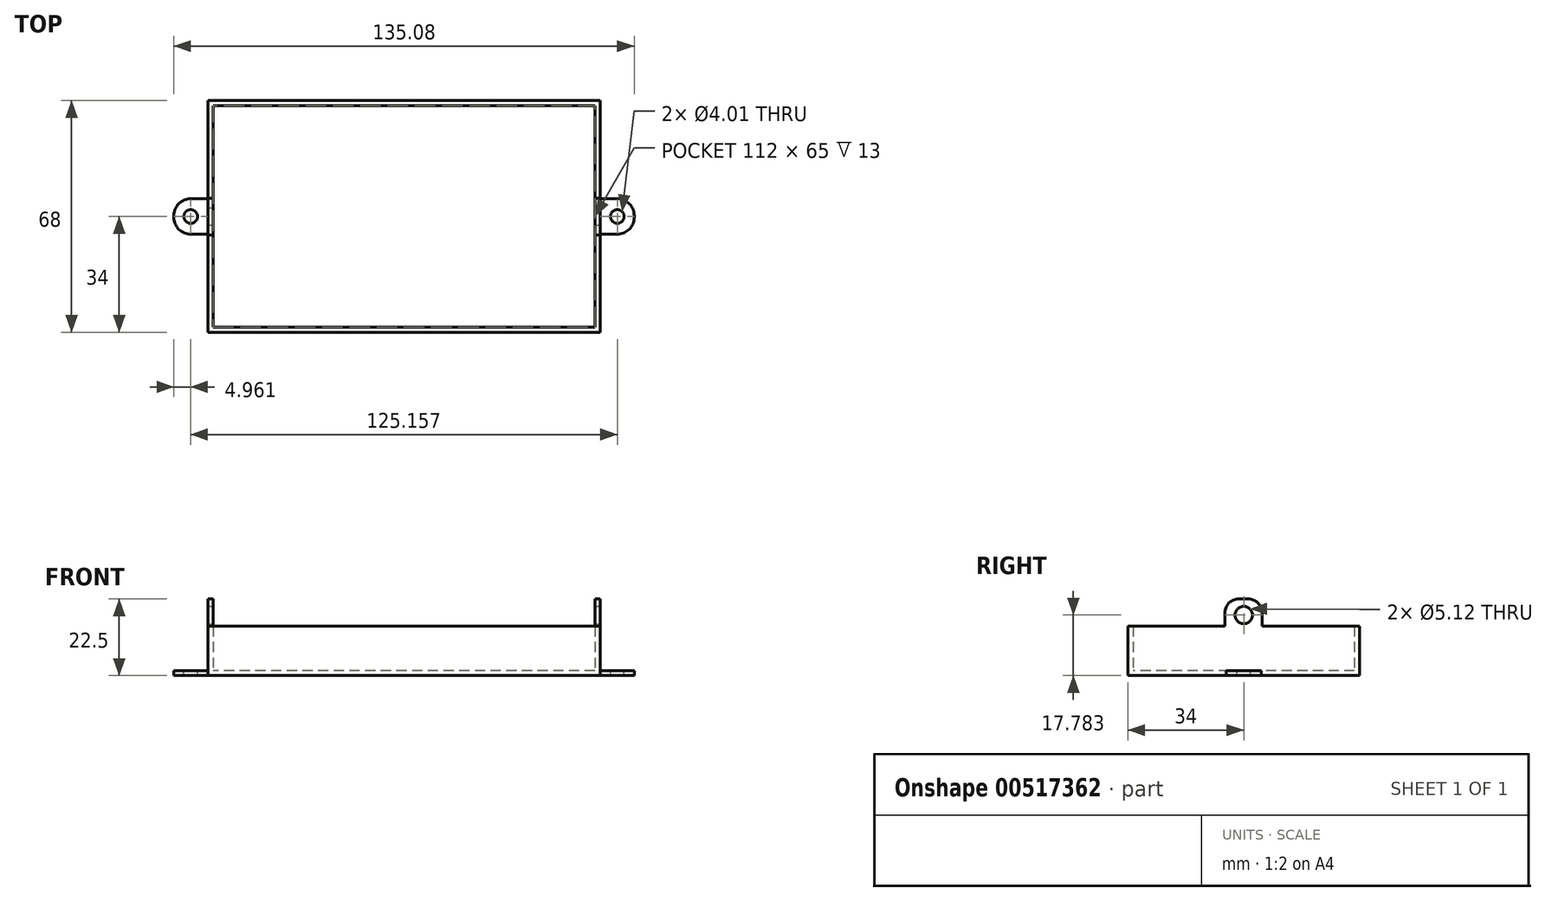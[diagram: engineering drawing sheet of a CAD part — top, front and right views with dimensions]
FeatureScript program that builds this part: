
annotation { "Feature Type Name" : "Feature", "Feature Type Description" : "" }
export const myFeature = defineFeature(function(context is Context, id is Id, definition is map)
    precondition{}
    {
        {
            var Q0;
            Q0=qCreatedBy(makeId("Top.planeOp"),FACE);
            var sketch = newSketch(context, id + "F0", { "sketchPlane" : qUnion([Q0])});
            skLineSegment(sketch, "E0.bottom", {"start": v(57.5, 34) * mm, "end": v(-57.5, 34) * mm});
            skLineSegment(sketch, "E0.top", {"start": v(57.5, -34) * mm, "end": v(-57.5, -34) * mm});
            skLineSegment(sketch, "E0.left", {"start": v(57.5, 34) * mm, "end": v(57.5, -34) * mm});
            skLineSegment(sketch, "E0.right", {"start": v(-57.5, 34) * mm, "end": v(-57.5, -34) * mm});
            skPoint(sketch, "E0.middle", {"position": v(0, 0) * mm});
            skLineSegment(sketch, "E1.top", {"start": v(57.5, 5.2) * mm, "end": v(67.54, 5.2) * mm});
            skLineSegment(sketch, "E1.left", {"start": v(57.5, 0) * mm, "end": v(57.5, 5.2) * mm});
            skLineSegment(sketch, "E1.right", {"start": v(67.54, 0) * mm, "end": v(67.54, 5.2) * mm});
            skLineSegment(sketch, "E2.MirrorCS", {"start": v(57.5, -5.2) * mm, "end": v(67.54, -5.2) * mm});
            skLineSegment(sketch, "E3.MirrorCS", {"start": v(67.54, 0) * mm, "end": v(67.54, -5.2) * mm});
            skLineSegment(sketch, "E4.MirrorCS", {"start": v(-57.5, 5.2) * mm, "end": v(-67.54, 5.2) * mm});
            skLineSegment(sketch, "E5.MirrorCS", {"start": v(-67.54, 0) * mm, "end": v(-67.54, 5.2) * mm});
            skLineSegment(sketch, "E6.MirrorCS", {"start": v(-67.54, 0) * mm, "end": v(-67.54, -5.2) * mm});
            skLineSegment(sketch, "E7.MirrorCS", {"start": v(-57.5, -5.2) * mm, "end": v(-67.54, -5.2) * mm});
            skSolve(sketch);
        }
        {
            var Q0;
            {var subQ3=sQuery(id+"F0.wireOp",EDGE,"E0.bottom");Q0=makeQuery(id+"F0.imprint","IMPRINT",FACE,{"disambiguationData":[TD([[makeQuery(id+"F0.imprint","IMPRINT",EDGE,{"derivedFrom":subQ3}),1.0]])]});}
            var Q1;
            {var subQ0=sQuery(id+"F0.wireOp",EDGE,"E4.MirrorCS");Q1=makeQuery(id+"F0.imprint","IMPRINT",FACE,{"disambiguationData":[TD([[makeQuery(id+"F0.imprint","IMPRINT",EDGE,{"derivedFrom":subQ0}),1.0]])]});}
            var Q2;
            Q2=makeQuery(id+"F0.imprint","IMPRINT",FACE,{"disambiguationData":[TD([[makeQuery(id+"F0.imprint","IMPRINT",EDGE,{"derivedFrom":sQuery(id+"F0.wireOp",EDGE,"E1.top")}),-1.0]])]});
            extrude(context, id + "F1", {"entities" : qUnion([Q0, Q1, Q2]), "depth" : 1.5 * mm, "offsetDistance" : 25 * mm});
        }
        {
            var Q0;
            Q0=makeQuery(id+"F1.opExtrude","CAP_FACE",FACE,{"disambiguationData":[OSD([sQuery(id+"F0.wireOp",EDGE,"E0.bottom"),sQuery(id+"F0.wireOp",EDGE,"E0.top"),sQuery(id+"F0.wireOp",EDGE,"E0.left"),sQuery(id+"F0.wireOp",EDGE,"E0.right"),sQuery(id+"F0.wireOp",EDGE,"E1.top"),sQuery(id+"F0.wireOp",EDGE,"E1.right"),sQuery(id+"F0.wireOp",EDGE,"E2.MirrorCS"),sQuery(id+"F0.wireOp",EDGE,"E3.MirrorCS"),sQuery(id+"F0.wireOp",EDGE,"E4.MirrorCS"),sQuery(id+"F0.wireOp",EDGE,"E5.MirrorCS"),sQuery(id+"F0.wireOp",EDGE,"E6.MirrorCS"),sQuery(id+"F0.wireOp",EDGE,"E7.MirrorCS")])],"isStart":false});
            var sketch = newSketch(context, id + "F2", { "sketchPlane" : qUnion([Q0])});
            skLineSegment(sketch, "E8", {"start": v(-57.5, 5.2) * mm, "end": v(-57.5, -5.2) * mm});
            skLineSegment(sketch, "E9", {"start": v(57.5, -5.2) * mm, "end": v(57.5, 5.2) * mm});
            skLineSegment(sketch, "E10.0", {"start": v(56, 32.5) * mm, "end": v(56, 5.2) * mm});
            skLineSegment(sketch, "E10.1", {"start": v(56, -5.2) * mm, "end": v(56, 5.2) * mm});
            skLineSegment(sketch, "E10.2", {"start": v(56, 32.5) * mm, "end": v(-56, 32.5) * mm});
            skLineSegment(sketch, "E10.3", {"start": v(56, -5.2) * mm, "end": v(56, -32.5) * mm});
            skLineSegment(sketch, "E10.4", {"start": v(-56, 32.5) * mm, "end": v(-56, 5.2) * mm});
            skLineSegment(sketch, "E10.5", {"start": v(-56, 5.2) * mm, "end": v(-56, -5.2) * mm});
            skLineSegment(sketch, "E10.6", {"start": v(-56, -5.2) * mm, "end": v(-56, -32.5) * mm});
            skLineSegment(sketch, "E10.7", {"start": v(56, -32.5) * mm, "end": v(-56, -32.5) * mm});
            skSolve(sketch);
        }
        {
            var Q0;
            Q0=makeQuery(id+"F2.imprint","IMPRINT",FACE,{"disambiguationData":[TD([[makeQuery(id+"F2.imprint","IMPRINT",EDGE,{"derivedFrom":sQuery(id+"F2.wireOp",EDGE,"E8")}),1.0]])]});
            extrude(context, id + "F3", {"entities" : qUnion([Q0]), "operationType" : NewBodyOperationType.ADD, "depth" : 13 * mm, "offsetDistance" : 25 * mm});
        }
        {
            var Q0;
            {var subQ0=sQuery(id+"F0.wireOp",EDGE,"E6.MirrorCS");var subQ1=sQuery(id+"F0.wireOp",EDGE,"E5.MirrorCS");var subQ2=sQuery(id+"F0.wireOp",EDGE,"E0.right");var subQ3=sQuery(id+"F0.wireOp",EDGE,"E0.top");var subQ4=sQuery(id+"F0.wireOp",EDGE,"E7.MirrorCS");var subQ5=sQuery(id+"F0.wireOp",EDGE,"E4.MirrorCS");var subQ6=sQuery(id+"F0.wireOp",EDGE,"E0.bottom");Q0=makeQuery(id+"F3.boolean.opBoolean","SPLIT",FACE,{"disambiguationData":[TD([makeQuery(id+"F1.opExtrude","SWEPT_FACE",FACE,{"disambiguationData":[OSD([subQ5])]})])],"derivedFrom":makeQuery(id+"F1.opExtrude","CAP_FACE",FACE,{"disambiguationData":[OSD([subQ6,subQ3,sQuery(id+"F0.wireOp",EDGE,"E0.left"),subQ2,sQuery(id+"F0.wireOp",EDGE,"E1.top"),sQuery(id+"F0.wireOp",EDGE,"E1.right"),sQuery(id+"F0.wireOp",EDGE,"E2.MirrorCS"),sQuery(id+"F0.wireOp",EDGE,"E3.MirrorCS"),subQ5,subQ1,subQ0,subQ4])],"isStart":false})});}
            var sketch = newSketch(context, id + "F4", { "sketchPlane" : qUnion([Q0])});
            skCircle(sketch, "E11", {"center": v(-62.58, 0) * mm, "radius": 2 * mm});
            skPoint(sketch, "E11.centerSnap0", {"position": v(-67.54, 0) * mm});
            skCircle(sketch, "E12.MirrorC", {"center": v(62.58, 0) * mm, "radius": 2 * mm});
            skSolve(sketch);
        }
        {
            var Q0;
            Q0 = qSketchRegion(id + "F4", true);
            extrude(context, id + "F5", {"entities" : qUnion([Q0]), "operationType" : NewBodyOperationType.REMOVE, "oppositeDirection" : true, "depth" : 2 * mm, "offsetDistance" : 25 * mm});
        }
        {
            var Q0;
            Q0=makeQuery(id+"F1.opExtrude","SWEPT_EDGE",EDGE,{"disambiguationData":[OSD([sQuery(id+"F0.wireOp",EDGE,"E4.MirrorCS"),sQuery(id+"F0.wireOp",EDGE,"E5.MirrorCS")])]});
            var Q1;
            Q1=makeQuery(id+"F1.opExtrude","SWEPT_EDGE",EDGE,{"disambiguationData":[OSD([sQuery(id+"F0.wireOp",EDGE,"E6.MirrorCS"),sQuery(id+"F0.wireOp",EDGE,"E7.MirrorCS")])]});
            var Q2;
            Q2=makeQuery(id+"F1.opExtrude","SWEPT_EDGE",EDGE,{"disambiguationData":[OSD([sQuery(id+"F0.wireOp",EDGE,"E1.top"),sQuery(id+"F0.wireOp",EDGE,"E1.right")])]});
            var Q3;
            Q3=makeQuery(id+"F1.opExtrude","SWEPT_EDGE",EDGE,{"disambiguationData":[OSD([sQuery(id+"F0.wireOp",EDGE,"E2.MirrorCS"),sQuery(id+"F0.wireOp",EDGE,"E3.MirrorCS")])]});
            fillet(context, id + "F6", {"entities" : qUnion([Q0, Q1, Q2, Q3]), "radius" : 5 * mm, "tangentPropagation" : true, "allowEdgeOverflow" : false});
        }
        {
            var Q0;
            Q0=makeQuery(id+"F3.opExtrude","CAP_FACE",FACE,{"disambiguationData":[OSD([sQuery(id+"F0.wireOp",EDGE,"E0.bottom"),sQuery(id+"F0.wireOp",EDGE,"E0.top"),sQuery(id+"F0.wireOp",EDGE,"E0.left"),sQuery(id+"F0.wireOp",EDGE,"E0.right"),sQuery(id+"F2.wireOp",EDGE,"E8"),sQuery(id+"F2.wireOp",EDGE,"E9"),sQuery(id+"F2.wireOp",EDGE,"E10.0"),sQuery(id+"F2.wireOp",EDGE,"E10.1"),sQuery(id+"F2.wireOp",EDGE,"E10.2"),sQuery(id+"F2.wireOp",EDGE,"E10.3"),sQuery(id+"F2.wireOp",EDGE,"E10.4"),sQuery(id+"F2.wireOp",EDGE,"E10.5"),sQuery(id+"F2.wireOp",EDGE,"E10.6"),sQuery(id+"F2.wireOp",EDGE,"E10.7")])],"isStart":false});
            var sketch = newSketch(context, id + "F7", { "sketchPlane" : qUnion([Q0])});
            skLineSegment(sketch, "E13", {"start": v(-57.5, 5.36) * mm, "end": v(-56, 5.36) * mm});
            skLineSegment(sketch, "E14", {"start": v(-57.5, -5.5) * mm, "end": v(-56, -5.5) * mm});
            skLineSegment(sketch, "E15", {"start": v(-56, 5.36) * mm, "end": v(-56, -5.5) * mm});
            skLineSegment(sketch, "E16", {"start": v(-57.5, -5.5) * mm, "end": v(-57.5, 5.36) * mm});
            skLineSegment(sketch, "E17.MirrorCS", {"start": v(56, 5.36) * mm, "end": v(56, -5.5) * mm});
            skLineSegment(sketch, "E18.MirrorCS", {"start": v(57.5, -5.5) * mm, "end": v(57.5, 5.36) * mm});
            skLineSegment(sketch, "E19.MirrorCS", {"start": v(57.5, 5.36) * mm, "end": v(56, 5.36) * mm});
            skLineSegment(sketch, "E20.MirrorCS", {"start": v(57.5, -5.5) * mm, "end": v(56, -5.5) * mm});
            skSolve(sketch);
        }
        {
            var Q0;
            Q0 = qSketchRegion(id + "F7", true);
            extrude(context, id + "F8", {"entities" : qUnion([Q0]), "operationType" : NewBodyOperationType.ADD, "depth" : 8 * mm, "offsetDistance" : 25 * mm});
        }
        {
            var Q0;
            Q0=makeQuery(id+"F8.opExtrude","CAP_EDGE",EDGE,{"disambiguationData":[OSD([sQuery(id+"F7.wireOp",EDGE,"E14")])],"isStart":false});
            var Q1;
            Q1=makeQuery(id+"F8.opExtrude","CAP_EDGE",EDGE,{"disambiguationData":[OSD([sQuery(id+"F7.wireOp",EDGE,"E13")])],"isStart":false});
            var Q2;
            Q2=makeQuery(id+"F8.opExtrude","CAP_EDGE",EDGE,{"disambiguationData":[OSD([sQuery(id+"F7.wireOp",EDGE,"E20.MirrorCS")])],"isStart":false});
            var Q3;
            Q3=makeQuery(id+"F8.opExtrude","CAP_EDGE",EDGE,{"disambiguationData":[OSD([sQuery(id+"F7.wireOp",EDGE,"E19.MirrorCS")])],"isStart":false});
            fillet(context, id + "F9", {"entities" : qUnion([Q0, Q1, Q2, Q3]), "radius" : 4 * mm, "tangentPropagation" : true, "allowEdgeOverflow" : false});
        }
        {
            var Q0;
            {var subQ0=sQuery(id+"F0.wireOp",EDGE,"E0.left");Q0=makeQuery(id+"F8.boolean.opBoolean","MERGE",FACE,{"derivedFrom":[makeQuery(id+"F3.boolean.opBoolean","MERGE",FACE,{"derivedFrom":[makeQuery(id+"F1.opExtrude","SWEPT_FACE",FACE,{"disambiguationData":[OSD([subQ0]),TDD([makeQuery(id+"F0.imprint","IMPRINT",EDGE,{"disambiguationData":[TD([[makeQuery(id+"F0.imprint","INTERSECT",VERTEX,{"derivedFrom":[sQuery(id+"F0.wireOp",EDGE,"E0.bottom"),subQ0]}),-1.0]])],"derivedFrom":subQ0})])]}),makeQuery(id+"F1.opExtrude","SWEPT_FACE",FACE,{"disambiguationData":[OSD([subQ0]),TDD([makeQuery(id+"F0.imprint","IMPRINT",EDGE,{"disambiguationData":[TD([[makeQuery(id+"F0.imprint","INTERSECT",VERTEX,{"derivedFrom":[sQuery(id+"F0.wireOp",EDGE,"E0.top"),subQ0]}),1.0]])],"derivedFrom":subQ0})])]}),makeQuery(id+"F3.opExtrude","SWEPT_FACE",FACE,{"disambiguationData":[OSD([subQ0,sQuery(id+"F2.wireOp",EDGE,"E9")])]})]}),makeQuery(id+"F8.opExtrude","SWEPT_FACE",FACE,{"disambiguationData":[OSD([sQuery(id+"F7.wireOp",EDGE,"E18.MirrorCS")])]})]});}
            var sketch = newSketch(context, id + "F10", { "sketchPlane" : qUnion([Q0])});
            skCircle(sketch, "E21", {"center": v(0, 17.78) * mm, "radius": 2.56 * mm});
            skSolve(sketch);
        }
        {
            var Q0;
            Q0 = qSketchRegion(id + "F10", true);
            extrude(context, id + "F11", {"entities" : qUnion([Q0]), "operationType" : NewBodyOperationType.REMOVE, "oppositeDirection" : true, "depth" : 125 * mm, "offsetDistance" : 25 * mm});
        }
    });
